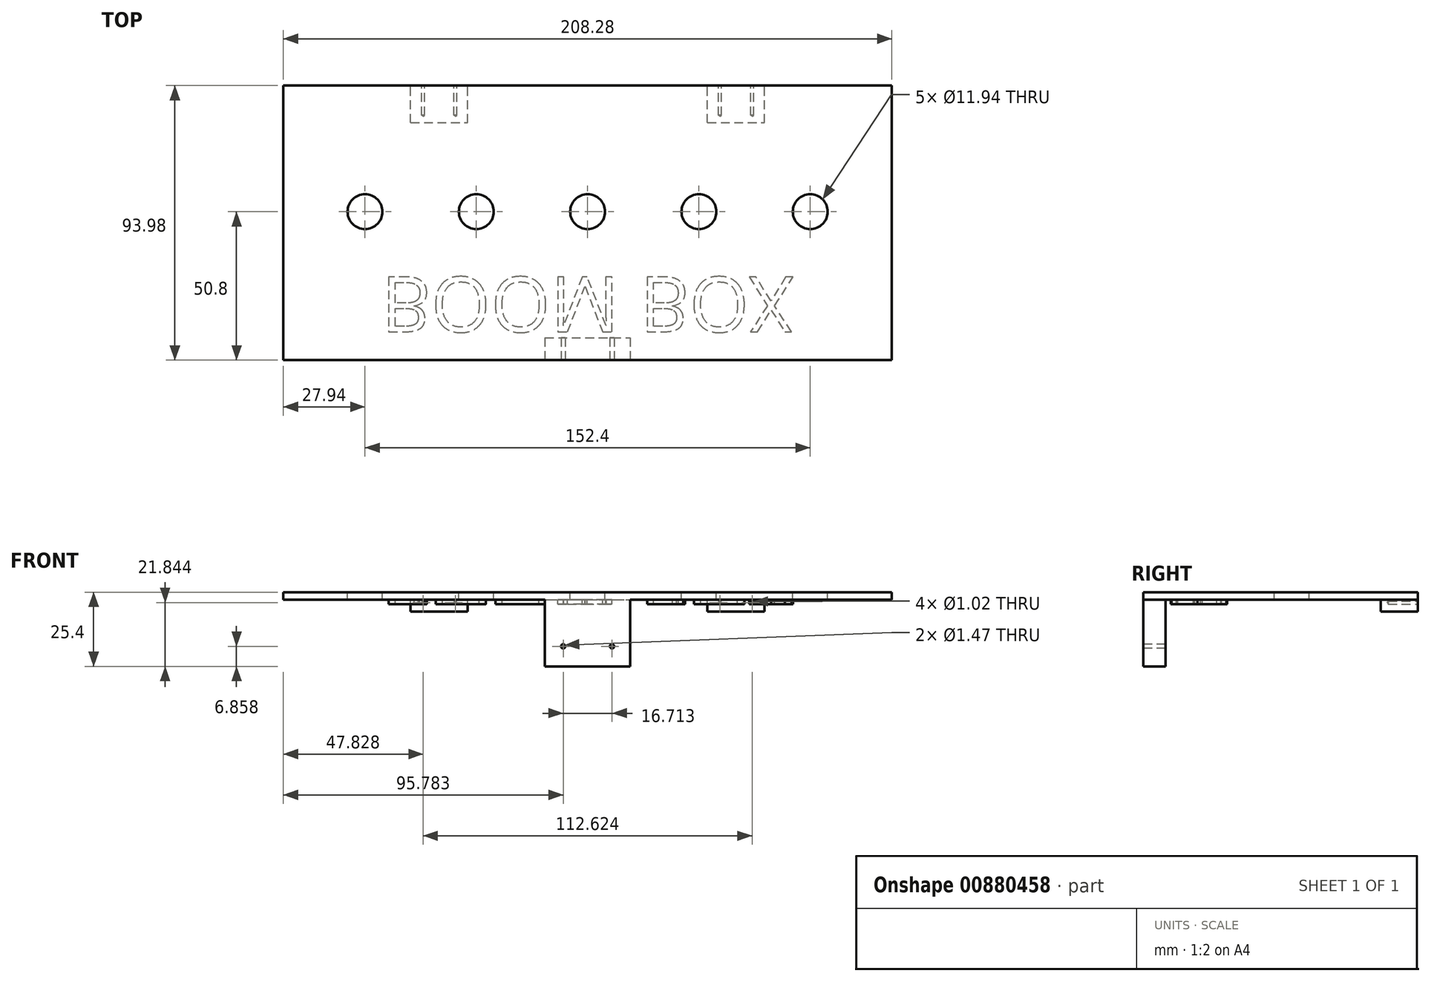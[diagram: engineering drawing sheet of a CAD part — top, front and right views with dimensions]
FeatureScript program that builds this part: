
annotation { "Feature Type Name" : "Feature", "Feature Type Description" : "" }
export const myFeature = defineFeature(function(context is Context, id is Id, definition is map)
    precondition{}
    {
        {
            var Q0;
            Q0=qCreatedBy(makeId("Top.planeOp"),FACE);
            var sketch = newSketch(context, id + "F0", { "sketchPlane" : qUnion([Q0])});
            skLineSegment(sketch, "E0.bottom", {"start": v(-104.14, -47) * mm, "end": v(104.14, -47) * mm});
            skLineSegment(sketch, "E0.top", {"start": v(-104.14, 47) * mm, "end": v(104.14, 47) * mm});
            skLineSegment(sketch, "E0.left", {"start": v(-104.14, -47) * mm, "end": v(-104.14, 47) * mm});
            skLineSegment(sketch, "E0.right", {"start": v(104.14, -47) * mm, "end": v(104.14, 47) * mm});
            skPoint(sketch, "E0.middle", {"position": v(0, 0) * mm});
            skSolve(sketch);
        }
        {
            var Q0;
            Q0=makeQuery(id+"F0.imprint","IMPRINT",FACE,{"disambiguationData":[TD([[makeQuery(id+"F0.imprint","IMPRINT",EDGE,{"derivedFrom":sQuery(id+"F0.wireOp",EDGE,"E0.bottom")}),1.0]])]});
            extrude(context, id + "F1", {"entities" : qUnion([Q0]), "depth" : 2.54 * mm, "offsetDistance" : 25.4 * mm});
        }
        {
            var Q0;
            Q0=makeQuery(id+"F1.opExtrude","CAP_FACE",FACE,{"disambiguationData":[OSD([sQuery(id+"F0.wireOp",EDGE,"E0.bottom"),sQuery(id+"F0.wireOp",EDGE,"E0.top"),sQuery(id+"F0.wireOp",EDGE,"E0.left"),sQuery(id+"F0.wireOp",EDGE,"E0.right")])],"isStart":false});
            var sketch = newSketch(context, id + "F2", { "sketchPlane" : qUnion([Q0])});
            skLineSegment(sketch, "E1", {"start": v(-104.14, 3.8) * mm, "end": v(104.14, 3.8) * mm, "construction": true});
            skPoint(sketch, "E2", {"position": v(0, 0) * mm});
            skPoint(sketch, "E3", {"position": v(-38.1, 3.8) * mm});
            skPoint(sketch, "E4", {"position": v(-76.2, 3.8) * mm});
            skPoint(sketch, "E5", {"position": v(38.1, 3.8) * mm});
            skPoint(sketch, "E6", {"position": v(76.2, 3.8) * mm});
            skCircle(sketch, "E7", {"center": v(-76.2, 3.8) * mm, "radius": 5.97 * mm});
            skCircle(sketch, "E8", {"center": v(-38.1, 3.8) * mm, "radius": 5.97 * mm});
            skCircle(sketch, "E9", {"center": v(38.1, 3.8) * mm, "radius": 5.97 * mm});
            skCircle(sketch, "E10", {"center": v(76.2, 3.8) * mm, "radius": 5.97 * mm});
            skLineSegment(sketch, "E11", {"start": v(0, 47) * mm, "end": v(-50.8, 47) * mm});
            skLineSegment(sketch, "E12", {"start": v(0, 47) * mm, "end": v(50.8, 47) * mm});
            skLineSegment(sketch, "E13.bottom", {"start": v(-60.58, 34.3) * mm, "end": v(-41.02, 34.3) * mm});
            skLineSegment(sketch, "E13.top", {"start": v(-60.58, 59.7) * mm, "end": v(-41.02, 59.7) * mm});
            skLineSegment(sketch, "E13.left", {"start": v(-60.58, 34.3) * mm, "end": v(-60.58, 59.7) * mm});
            skLineSegment(sketch, "E13.right", {"start": v(-41.02, 34.3) * mm, "end": v(-41.02, 59.7) * mm});
            skPoint(sketch, "E13.middle", {"position": v(-50.8, 47) * mm});
            skLineSegment(sketch, "E14.bottom", {"start": v(41.02, 34.3) * mm, "end": v(60.58, 34.3) * mm});
            skLineSegment(sketch, "E14.top", {"start": v(41.02, 59.7) * mm, "end": v(60.58, 59.7) * mm});
            skLineSegment(sketch, "E14.left", {"start": v(41.02, 34.3) * mm, "end": v(41.02, 59.7) * mm});
            skLineSegment(sketch, "E14.right", {"start": v(60.58, 34.3) * mm, "end": v(60.58, 59.7) * mm});
            skPoint(sketch, "E14.middle", {"position": v(50.8, 47) * mm});
            skCircle(sketch, "E15", {"center": v(0, 3.8) * mm, "radius": 5.97 * mm});
            skLineSegment(sketch, "E16.bottom", {"start": v(-14.6, -39.37) * mm, "end": v(14.6, -39.37) * mm});
            skLineSegment(sketch, "E16.top", {"start": v(-14.6, -47) * mm, "end": v(14.6, -47) * mm});
            skLineSegment(sketch, "E16.left", {"start": v(-14.6, -39.37) * mm, "end": v(-14.6, -47) * mm});
            skLineSegment(sketch, "E16.right", {"start": v(14.6, -39.37) * mm, "end": v(14.6, -47) * mm});
            skSolve(sketch);
        }
        {
            var Q0;
            Q0=makeQuery(id+"F2.imprint","IMPRINT",FACE,{"disambiguationData":[TD([[makeQuery(id+"F2.imprint","IMPRINT",EDGE,{"derivedFrom":sQuery(id+"F2.wireOp",EDGE,"E7")}),1.0]])]});
            var Q1;
            Q1=makeQuery(id+"F2.imprint","IMPRINT",FACE,{"disambiguationData":[TD([[makeQuery(id+"F2.imprint","IMPRINT",EDGE,{"derivedFrom":sQuery(id+"F2.wireOp",EDGE,"E8")}),1.0]])]});
            var Q2;
            Q2=makeQuery(id+"F2.imprint","IMPRINT",FACE,{"disambiguationData":[TD([[makeQuery(id+"F2.imprint","IMPRINT",EDGE,{"derivedFrom":sQuery(id+"F2.wireOp",EDGE,"WjX7iTg2-eBNJ-bVMp-4ENW-5L5RIgl6nJnl")}),1.0]])]});
            var Q3;
            Q3=makeQuery(id+"F2.imprint","IMPRINT",FACE,{"disambiguationData":[TD([[makeQuery(id+"F2.imprint","IMPRINT",EDGE,{"derivedFrom":sQuery(id+"F2.wireOp",EDGE,"E9")}),1.0]])]});
            var Q4;
            Q4=makeQuery(id+"F2.imprint","IMPRINT",FACE,{"disambiguationData":[TD([[makeQuery(id+"F2.imprint","IMPRINT",EDGE,{"derivedFrom":sQuery(id+"F2.wireOp",EDGE,"E10")}),1.0]])]});
            var Q5;
            {var subQ1=sQuery(id+"F2.wireOp",EDGE,"E13.top");Q5=makeQuery(id+"F2.imprint","IMPRINT",FACE,{"disambiguationData":[TD([[makeQuery(id+"F2.imprint","IMPRINT",EDGE,{"derivedFrom":subQ1}),-1.0]])]});}
            var Q6;
            {var subQ1=sQuery(id+"F2.wireOp",EDGE,"E14.top");Q6=makeQuery(id+"F2.imprint","IMPRINT",FACE,{"disambiguationData":[TD([[makeQuery(id+"F2.imprint","IMPRINT",EDGE,{"derivedFrom":subQ1}),-1.0]])]});}
            var Q7;
            Q7=makeQuery(id+"F2.imprint","IMPRINT",FACE,{"disambiguationData":[TD([[makeQuery(id+"F2.imprint","IMPRINT",EDGE,{"derivedFrom":sQuery(id+"F2.wireOp",EDGE,"E15")}),1.0]])]});
            extrude(context, id + "F3", {"entities" : qUnion([Q0, Q1, Q2, Q3, Q4, Q5, Q6, Q7]), "operationType" : NewBodyOperationType.REMOVE, "endBound" : BoundingType.THROUGH_ALL, "oppositeDirection" : true, "depth" : 25.4 * mm, "offsetDistance" : 25.4 * mm});
        }
        {
            var Q0;
            {var subQ1=sQuery(id+"F2.wireOp",EDGE,"E13.bottom");Q0=makeQuery(id+"F2.imprint","IMPRINT",FACE,{"disambiguationData":[TD([[makeQuery(id+"F2.imprint","IMPRINT",EDGE,{"derivedFrom":subQ1}),1.0]])]});}
            var Q1;
            {var subQ1=sQuery(id+"F2.wireOp",EDGE,"E14.bottom");Q1=makeQuery(id+"F2.imprint","IMPRINT",FACE,{"disambiguationData":[TD([[makeQuery(id+"F2.imprint","IMPRINT",EDGE,{"derivedFrom":subQ1}),1.0]])]});}
            extrude(context, id + "F4", {"entities" : qUnion([Q0, Q1]), "operationType" : NewBodyOperationType.ADD, "oppositeDirection" : true, "depth" : 6.6 * mm, "offsetDistance" : 25.4 * mm});
        }
        {
            var Q0;
            Q0=makeQuery(id+"F2.imprint","IMPRINT",FACE,{"disambiguationData":[TD([[makeQuery(id+"F2.imprint","IMPRINT",EDGE,{"derivedFrom":sQuery(id+"F2.wireOp",EDGE,"E16.bottom")}),-1.0]])]});
            extrude(context, id + "F5", {"entities" : qUnion([Q0]), "operationType" : NewBodyOperationType.ADD, "oppositeDirection" : true, "depth" : 25.4 * mm, "offsetDistance" : 25.4 * mm});
        }
        {
            var Q0;
            {var subQ0=sQuery(id+"F0.wireOp",EDGE,"E0.top");Q0=makeQuery(id+"F4.boolean.opBoolean","MERGE",FACE,{"derivedFrom":[makeQuery(id+"F1.opExtrude","SWEPT_FACE",FACE,{"disambiguationData":[OSD([subQ0])]}),makeQuery(id+"F4.opExtrude","SWEPT_FACE",FACE,{"disambiguationData":[OSD([subQ0,sQuery(id+"F2.wireOp",EDGE,"E11")])]}),makeQuery(id+"F4.opExtrude","SWEPT_FACE",FACE,{"disambiguationData":[OSD([subQ0,sQuery(id+"F2.wireOp",EDGE,"E12")])]})]});}
            var sketch = newSketch(context, id + "F6", { "sketchPlane" : qUnion([Q0])});
            skLineSegment(sketch, "E17", {"start": v(-60.58, -1.02) * mm, "end": v(-41.02, -1.02) * mm, "construction": true});
            skLineSegment(sketch, "E18", {"start": v(41.02, -1.02) * mm, "end": v(60.58, -1.02) * mm, "construction": true});
            skPoint(sketch, "E19", {"position": v(-50.8, -1.02) * mm});
            skPoint(sketch, "E20", {"position": v(50.8, -1.02) * mm});
            skPoint(sketch, "E21", {"position": v(-56.31, -1.02) * mm});
            skPoint(sketch, "E22", {"position": v(-45.29, -1.02) * mm});
            skPoint(sketch, "E23", {"position": v(45.29, -1.02) * mm});
            skPoint(sketch, "E24", {"position": v(56.31, -1.02) * mm});
            skSolve(sketch);
        }
        {
            var Q0;
            Q0=sQuery(id+"F6.wireOp",VERTEX,"E21");
            var Q1;
            Q1=sQuery(id+"F6.wireOp",VERTEX,"E22");
            var Q2;
            Q2=sQuery(id+"F6.wireOp",VERTEX,"E23");
            var Q3;
            Q3=sQuery(id+"F6.wireOp",VERTEX,"E24");
            var Q4;
            Q4=makeQuery(id+"F1.opExtrude","SWEPT_BODY",BODY,{"disambiguationData":[OSD([sQuery(id+"F0.wireOp",EDGE,"E0.bottom"),sQuery(id+"F0.wireOp",EDGE,"E0.top"),sQuery(id+"F0.wireOp",EDGE,"E0.left"),sQuery(id+"F0.wireOp",EDGE,"E0.right")])]});
            hole(context, id + "F7", {"style" : HoleStyle.SIMPLE, "endStyle" : HoleEndStyle.BLIND, "holeDiameter" : 1.02 * mm, "majorDiameter" : 6.35 * mm, "holeDepth" : 10.16 * mm, "isTappedThrough" : true, "tappedDepth" : 12.7 * mm, "tapClearance" : 3, "locations" : qUnion([Q0, Q1, Q2, Q3]), "scope" : qUnion([Q4])});
        }
        {
            var Q0;
            Q0=makeQuery(id+"F5.boolean.opBoolean","MERGE",FACE,{"derivedFrom":[makeQuery(id+"F1.opExtrude","SWEPT_FACE",FACE,{"disambiguationData":[OSD([sQuery(id+"F0.wireOp",EDGE,"E0.bottom")])]}),makeQuery(id+"F5.opExtrude","SWEPT_FACE",FACE,{"disambiguationData":[OSD([sQuery(id+"F2.wireOp",EDGE,"E16.top")])]})]});
            var sketch = newSketch(context, id + "F8", { "sketchPlane" : qUnion([Q0])});
            skLineSegment(sketch, "E25", {"start": v(0, -22.86) * mm, "end": v(0, 2.54) * mm, "construction": true});
            skLineSegment(sketch, "E26.bottom", {"start": v(-11.56, 0.25) * mm, "end": v(11.56, 0.25) * mm, "construction": true});
            skLineSegment(sketch, "E26.top", {"start": v(-11.56, -22.6) * mm, "end": v(11.56, -22.6) * mm, "construction": true});
            skLineSegment(sketch, "E26.left", {"start": v(-11.56, 0.25) * mm, "end": v(-11.56, -22.6) * mm, "construction": true});
            skLineSegment(sketch, "E26.right", {"start": v(11.56, 0.25) * mm, "end": v(11.56, -22.6) * mm, "construction": true});
            skPoint(sketch, "E26.middle", {"position": v(0, -11.18) * mm});
            skPoint(sketch, "E27", {"position": v(-8.36, -16) * mm});
            skPoint(sketch, "E28", {"position": v(8.36, -16) * mm});
            skSolve(sketch);
        }
        {
            var Q0;
            Q0=sQuery(id+"F8.wireOp",VERTEX,"E28");
            var Q1;
            Q1=sQuery(id+"F8.wireOp",VERTEX,"E27");
            var Q2;
            Q2=makeQuery(id+"F1.opExtrude","SWEPT_BODY",BODY,{"disambiguationData":[OSD([sQuery(id+"F0.wireOp",EDGE,"E0.bottom"),sQuery(id+"F0.wireOp",EDGE,"E0.top"),sQuery(id+"F0.wireOp",EDGE,"E0.left"),sQuery(id+"F0.wireOp",EDGE,"E0.right")])]});
            hole(context, id + "F9", {"style" : HoleStyle.SIMPLE, "endStyle" : HoleEndStyle.BLIND, "holeDiameter" : 1.47 * mm, "majorDiameter" : 6.35 * mm, "holeDepth" : 10.16 * mm, "isTappedThrough" : true, "tappedDepth" : 12.7 * mm, "tapClearance" : 3, "locations" : qUnion([Q0, Q1]), "scope" : qUnion([Q2])});
        }
        {
            var Q0;
            Q0=makeQuery(id+"F1.opExtrude","CAP_FACE",FACE,{"disambiguationData":[OSD([sQuery(id+"F0.wireOp",EDGE,"E0.bottom"),sQuery(id+"F0.wireOp",EDGE,"E0.top"),sQuery(id+"F0.wireOp",EDGE,"E0.left"),sQuery(id+"F0.wireOp",EDGE,"E0.right")])],"isStart":true});
            var sketch = newSketch(context, id + "F10", { "sketchPlane" : qUnion([Q0])});
            skText(sketch, "E29", { "text": "BOOM BOX", "fontName": "OpenSans-Regular.ttf"});
            const initialGuessF10  = {"E29": [-0.07063, 0.01858, 1, 0, 0.0189]};
            skSetInitialGuess(sketch, initialGuessF10);
            skSolve(sketch);
        }
        {
            var Q0;
            Q0 = qSketchRegion(id + "F10", true);
            extrude(context, id + "F11", {"entities" : qUnion([Q0]), "operationType" : NewBodyOperationType.ADD, "depth" : 1.52 * mm, "offsetDistance" : 25.4 * mm});
        }
    });
